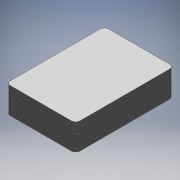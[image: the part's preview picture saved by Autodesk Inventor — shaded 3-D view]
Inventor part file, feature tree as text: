
AUTODESK INVENTOR PART (.ipt)
format: ipt  version: 2018 (Build 220112000, 112)  size: 641,536 bytes
history: native  units: mm
features: extrude x1, pattern_linear x1, sketch x1
ambient origin geometry x8: Origin, YZ Plane, XZ Plane, XY Plane, X Axis, Y Axis, Z Axis, Center Point
bodies: Solid1 (feature_tree)
feature tree (3):
  extrude  "Extrusion1"  Depth=89.0mm
  pattern_linear  "Rectangular Pattern1"  Spacing1=4.0mm  [1 undecoded]
  sketch  "Sketch1"  dims[d0=63.0mm d1=89.0mm d2=4.0mm d3=0.27mm d4=0.0mm d5=825.0mm d7=0.285762mm]
note: 1 required parameter value undecoded (feature->parameter linkage not recoverable at this tier; creation-order binding heuristic only, values carry confidence <= 0.55)
